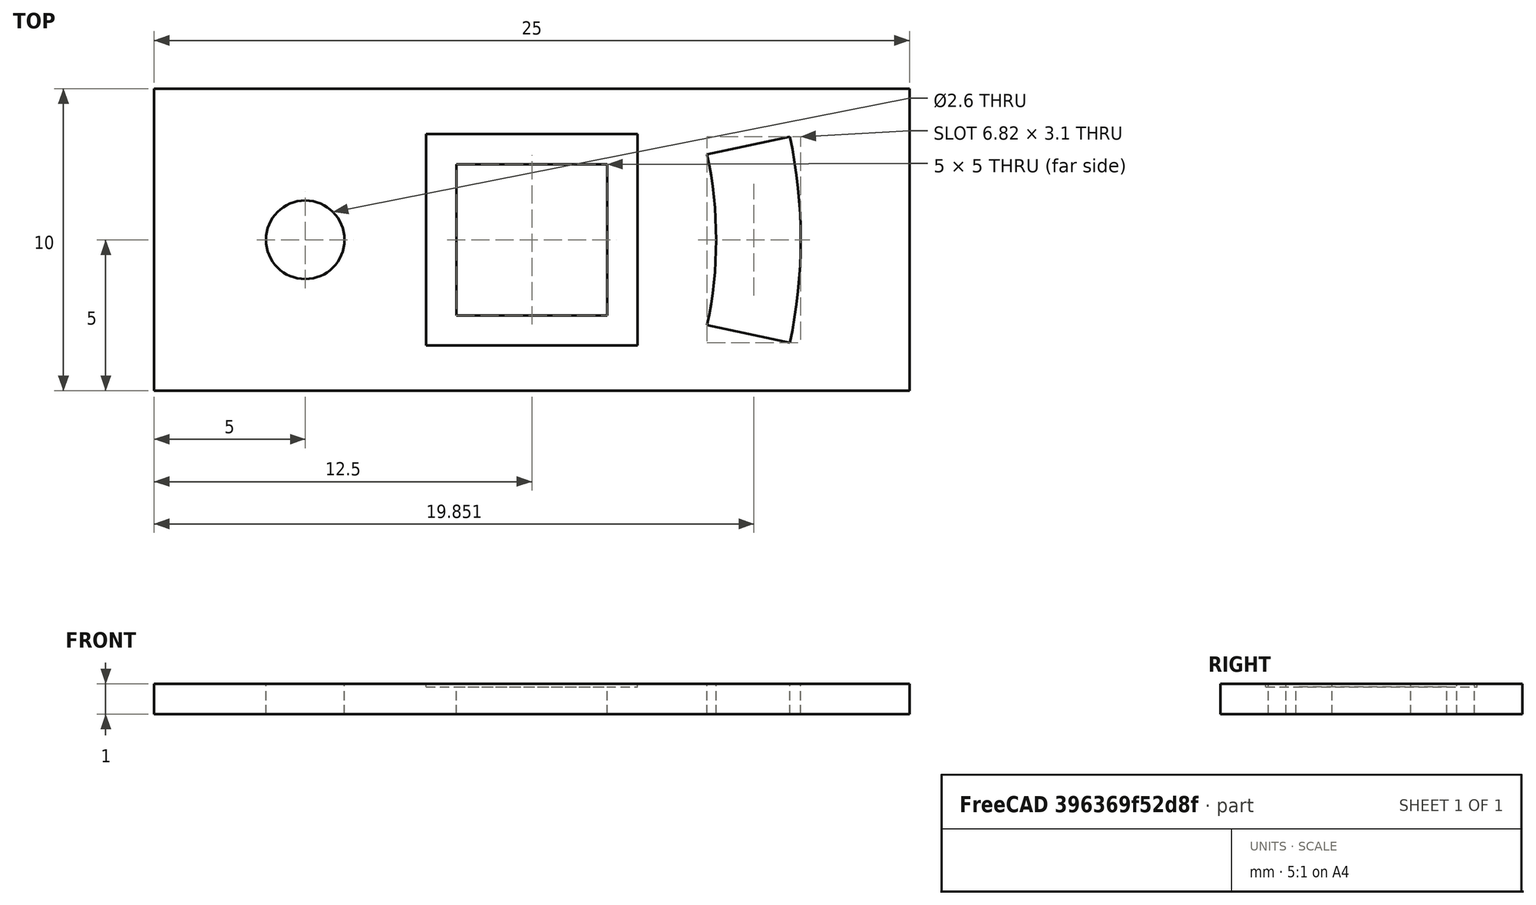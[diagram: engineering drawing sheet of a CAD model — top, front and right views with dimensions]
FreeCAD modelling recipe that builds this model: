
FCSTD DOCUMENT  (FreeCAD 0.15R4671 (Git))
Label: Gitterhalter2
License: All rights reserved
LicenseURL: http://en.wikipedia.org/wiki/All_rights_reserved
objects: Part::Cut×5, Part::Cylinder×3, Part::Box×3
note: 11 computed .brp shape members not serialized (recipe doc carries the construction recipe); baked Part::Feature solids carry a one-line shape summary decoded from their .brp

FEATURE [Part::Cylinder] Cylinder  label="Zylinder"
  Angle = 360
  Height = 10
  Placement = pos=(5,5,0) rot=(0,0,1;0rad)
  Radius = 1.3
FEATURE [Part::Box] Box  label="Würfel"
  Height = 1
  Length = 25
  Width = 10
FEATURE [Part::Cylinder] Cylinder001  label="Zylinder001"
  Angle = 24
  Height = 10
  Placement = pos=(3,5,0) rot=(0,0,-1;0.20944rad)
  Radius = 16.4
FEATURE [Part::Cylinder] Cylinder002  label="Zylinder002"
  Angle = 24
  Height = 11
  Placement = pos=(3,5,0) rot=(0,0,-1;0.20944rad)
  Radius = 13.6
FEATURE [Part::Cut] Cut
  Base = -> Cylinder001
  Placement = pos=(2,0,0) rot=(0,0,1;0rad)
  Tool = -> Cylinder002
FEATURE [Part::Box] Box001  label="Würfel001"
  Height = 2
  Length = 5
  Placement = pos=(10,2.5,0) rot=(0,0,1;0rad)
  Width = 5
FEATURE [Part::Box] Box002  label="Würfel002"
  Height = 0.5
  Length = 7
  Placement = pos=(9,1.5,0.9) rot=(0,0,1;0rad)
  Width = 7
FEATURE [Part::Cut] Cut001
  Base = -> Box
  Tool = -> Box001
FEATURE [Part::Cut] Cut002
  Base = -> Cut001
  Tool = -> Box002
FEATURE [Part::Cut] Cut003
  Base = -> Cut002
  Tool = -> Cylinder
FEATURE [Part::Cut] Cut004
  Base = -> Cut003
  Tool = -> Cut
